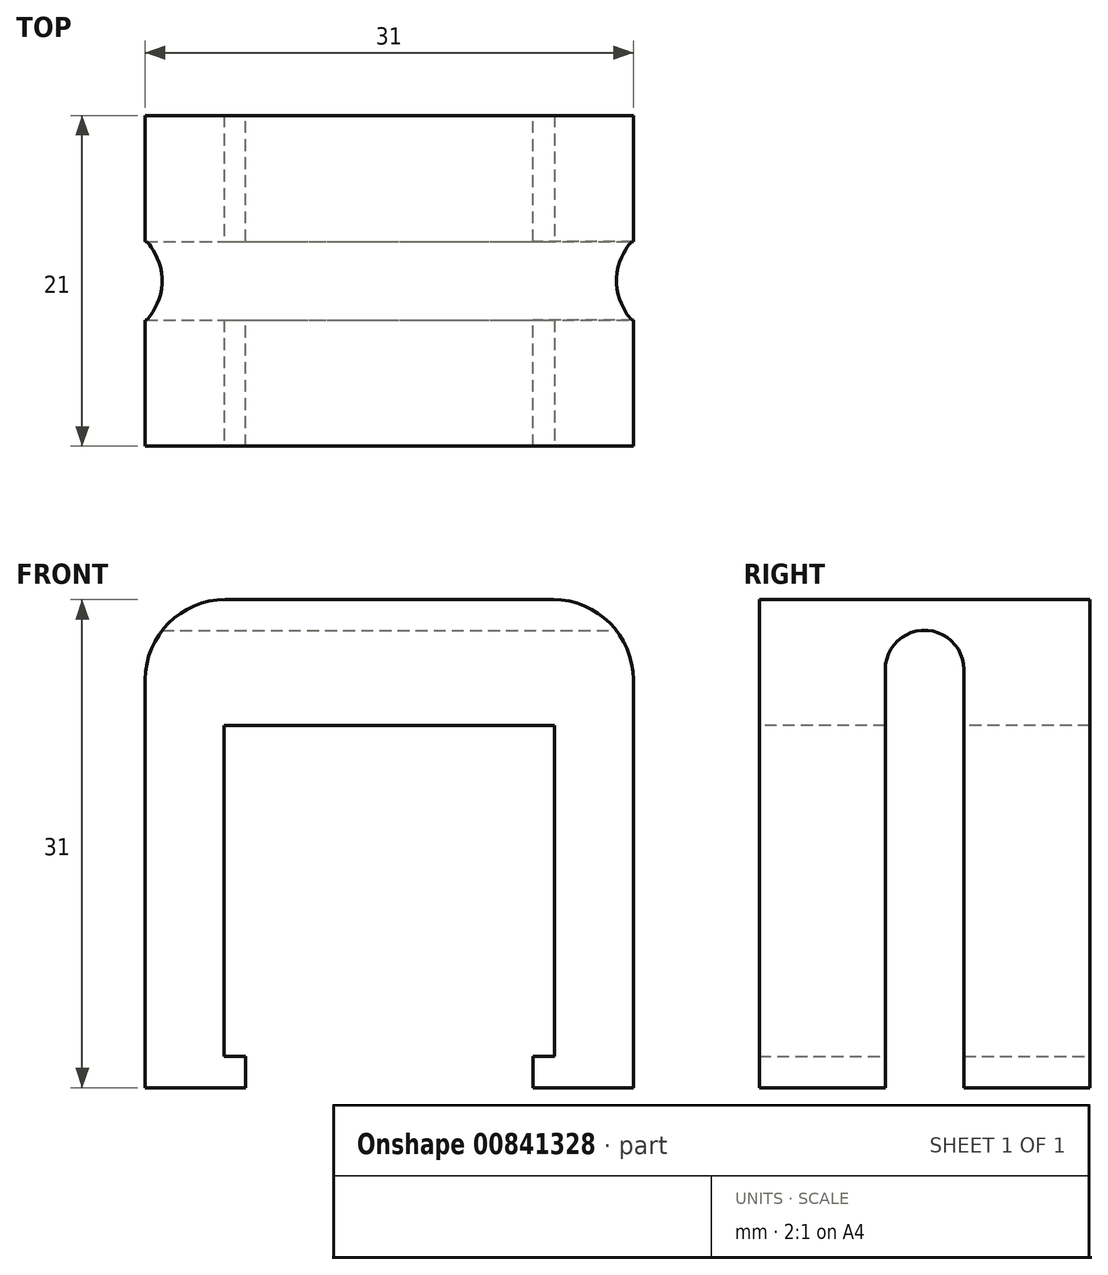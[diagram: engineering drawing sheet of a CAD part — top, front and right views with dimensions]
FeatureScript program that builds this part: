
annotation { "Feature Type Name" : "Feature", "Feature Type Description" : "" }
export const myFeature = defineFeature(function(context is Context, id is Id, definition is map)
    precondition{}
    {
        {
            var Q0;
            Q0=qCreatedBy(makeId("Top.planeOp"),FACE);
            var sketch = newSketch(context, id + "F0", { "sketchPlane" : qUnion([Q0])});
            skLineSegment(sketch, "E0.bottom", {"start": v(15.5, 10.5) * mm, "end": v(-15.5, 10.5) * mm});
            skLineSegment(sketch, "E0.top", {"start": v(15.5, -10.5) * mm, "end": v(-15.5, -10.5) * mm});
            skLineSegment(sketch, "E0.left", {"start": v(15.5, 10.5) * mm, "end": v(15.5, -10.5) * mm});
            skLineSegment(sketch, "E0.right", {"start": v(-15.5, 10.5) * mm, "end": v(-15.5, -10.5) * mm});
            skPoint(sketch, "E0.middle", {"position": v(0, 0) * mm});
            skSolve(sketch);
        }
        {
            var Q0;
            Q0=makeQuery(id+"F0.imprint","IMPRINT",FACE,{"disambiguationData":[TD([[makeQuery(id+"F0.imprint","IMPRINT",EDGE,{"derivedFrom":sQuery(id+"F0.wireOp",EDGE,"E0.bottom")}),1.0]])]});
            extrude(context, id + "F1", {"entities" : qUnion([Q0]), "depth" : 28 * mm, "offsetDistance" : 25.4 * mm});
        }
        {
            var Q0;
            Q0=qCreatedBy(makeId("Front.planeOp"),FACE);
            var sketch = newSketch(context, id + "F2", { "sketchPlane" : qUnion([Q0])});
            skLineSegment(sketch, "E1.bottom", {"start": v(10.5, 21) * mm, "end": v(-10.5, 21) * mm});
            skLineSegment(sketch, "E1.top", {"start": v(10.5, -21) * mm, "end": v(-10.5, -21) * mm});
            skLineSegment(sketch, "E1.left", {"start": v(10.5, 21) * mm, "end": v(10.5, -21) * mm});
            skLineSegment(sketch, "E1.right", {"start": v(-10.5, 21) * mm, "end": v(-10.5, -21) * mm});
            skPoint(sketch, "E1.middle", {"position": v(0, 0) * mm});
            skSolve(sketch);
        }
        {
            var Q0;
            Q0 = qSketchRegion(id + "F2", true);
            extrude(context, id + "F3", {"entities" : qUnion([Q0]), "operationType" : NewBodyOperationType.REMOVE, "oppositeDirection" : true, "depth" : 50.8 * mm, "offsetDistance" : 25.4 * mm});
        }
        {
            var Q0;
            Q0 = qSketchRegion(id + "F2", true);
            extrude(context, id + "F4", {"entities" : qUnion([Q0]), "operationType" : NewBodyOperationType.REMOVE, "depth" : 25.4 * mm, "offsetDistance" : 25.4 * mm});
        }
        {
            var Q0;
            Q0=qCreatedBy(makeId("Right.planeOp"),FACE);
            var sketch = newSketch(context, id + "F5", { "sketchPlane" : qUnion([Q0])});
            skCircle(sketch, "E2", {"center": v(0, 24.55) * mm, "radius": 2.5 * mm});
            skLineSegment(sketch, "E3.bottom", {"start": v(0, 24.55) * mm, "end": v(2.5, 24.55) * mm});
            skLineSegment(sketch, "E3.top", {"start": v(0, -28.56) * mm, "end": v(2.5, -28.56) * mm});
            skLineSegment(sketch, "E3.left", {"start": v(0, 24.55) * mm, "end": v(0, -28.56) * mm});
            skLineSegment(sketch, "E3.right", {"start": v(2.5, 24.55) * mm, "end": v(2.5, -28.56) * mm});
            skLineSegment(sketch, "E4.bottom", {"start": v(0, 24.55) * mm, "end": v(-2.5, 24.55) * mm});
            skLineSegment(sketch, "E4.top", {"start": v(0, -33.74) * mm, "end": v(-2.5, -33.74) * mm});
            skLineSegment(sketch, "E4.left", {"start": v(0, 24.55) * mm, "end": v(0, -33.74) * mm});
            skLineSegment(sketch, "E4.right", {"start": v(-2.5, 24.55) * mm, "end": v(-2.5, -33.74) * mm});
            skSolve(sketch);
        }
        {
            var Q0;
            Q0 = qSketchRegion(id + "F5", true);
            extrude(context, id + "F6", {"entities" : qUnion([Q0]), "operationType" : NewBodyOperationType.REMOVE, "oppositeDirection" : true, "depth" : 25.4 * mm, "offsetDistance" : 25.4 * mm});
        }
        {
            var Q0;
            Q0 = qSketchRegion(id + "F5", true);
            extrude(context, id + "F7", {"entities" : qUnion([Q0]), "operationType" : NewBodyOperationType.REMOVE, "depth" : 25.4 * mm, "offsetDistance" : 25.4 * mm});
        }
        {
            var Q0;
            {var subQ1=sQuery(id+"F0.wireOp",EDGE,"E0.left");var subQ2=sQuery(id+"F0.wireOp",EDGE,"E0.top");var subQ3=sQuery(id+"F0.wireOp",EDGE,"E0.bottom");Q0=makeQuery(id+"F4.boolean.opBoolean","SPLIT",FACE,{"disambiguationData":[TD([makeQuery(id+"F1.opExtrude","SWEPT_FACE",FACE,{"disambiguationData":[OSD([subQ1])]})])],"derivedFrom":makeQuery(id+"F1.opExtrude","CAP_FACE",FACE,{"disambiguationData":[OSD([subQ3,subQ2,subQ1,sQuery(id+"F0.wireOp",EDGE,"E0.right")])],"isStart":true})});}
            var Q1;
            {var subQ1=sQuery(id+"F0.wireOp",EDGE,"E0.top");var subQ2=sQuery(id+"F0.wireOp",EDGE,"E0.right");var subQ3=sQuery(id+"F0.wireOp",EDGE,"E0.bottom");Q1=makeQuery(id+"F4.boolean.opBoolean","SPLIT",FACE,{"disambiguationData":[TD([makeQuery(id+"F1.opExtrude","SWEPT_FACE",FACE,{"disambiguationData":[OSD([subQ2])]})])],"derivedFrom":makeQuery(id+"F1.opExtrude","CAP_FACE",FACE,{"disambiguationData":[OSD([subQ3,subQ1,sQuery(id+"F0.wireOp",EDGE,"E0.left"),subQ2])],"isStart":true})});}
            extrude(context, id + "F8", {"entities" : qUnion([Q0, Q1]), "operationType" : NewBodyOperationType.ADD, "depth" : 2 * mm, "offsetDistance" : 25.4 * mm});
        }
        {
            var Q0;
            Q0=qCreatedBy(makeId("Right.planeOp"),FACE);
            var sketch = newSketch(context, id + "F9", { "sketchPlane" : qUnion([Q0])});
            skLineSegment(sketch, "E5.bottom", {"start": v(0, 0) * mm, "end": v(-10.5, 0) * mm});
            skLineSegment(sketch, "E5.top", {"start": v(0, -2) * mm, "end": v(-10.5, -2) * mm});
            skLineSegment(sketch, "E5.left", {"start": v(0, 0) * mm, "end": v(0, -2) * mm});
            skLineSegment(sketch, "E5.right", {"start": v(-10.5, 0) * mm, "end": v(-10.5, -2) * mm});
            skLineSegment(sketch, "E6.bottom", {"start": v(0, 0) * mm, "end": v(10.5, 0) * mm});
            skLineSegment(sketch, "E6.top", {"start": v(0, -2) * mm, "end": v(10.5, -2) * mm});
            skLineSegment(sketch, "E6.right", {"start": v(10.5, 0) * mm, "end": v(10.5, -2) * mm});
            skSolve(sketch);
        }
        {
            var Q0;
            Q0=makeQuery(id+"F9.imprint","IMPRINT",FACE,{"disambiguationData":[TD([[makeQuery(id+"F9.imprint","IMPRINT",EDGE,{"derivedFrom":sQuery(id+"F9.wireOp",EDGE,"E5.bottom")}),1.0]])]});
            var Q1;
            Q1=makeQuery(id+"F9.imprint","IMPRINT",FACE,{"disambiguationData":[TD([[makeQuery(id+"F9.imprint","IMPRINT",EDGE,{"derivedFrom":sQuery(id+"F9.wireOp",EDGE,"E6.bottom")}),-1.0]])]});
            extrude(context, id + "F10", {"entities" : qUnion([Q0, Q1]), "operationType" : NewBodyOperationType.ADD, "depth" : 10.5 * mm, "offsetDistance" : 25.4 * mm});
        }
        {
            var Q0;
            Q0=makeQuery(id+"F10.opExtrude","CAP_FACE",FACE,{"disambiguationData":[OSD([sQuery(id+"F9.wireOp",EDGE,"E5.bottom"),sQuery(id+"F9.wireOp",EDGE,"E5.top"),sQuery(id+"F9.wireOp",EDGE,"E5.right"),sQuery(id+"F9.wireOp",EDGE,"E6.bottom"),sQuery(id+"F9.wireOp",EDGE,"E6.top"),sQuery(id+"F9.wireOp",EDGE,"E6.right")])],"isStart":true});
            extrude(context, id + "F11", {"entities" : qUnion([Q0]), "operationType" : NewBodyOperationType.ADD, "depth" : 10.5 * mm, "offsetDistance" : 25.4 * mm});
        }
        {
            var Q0;
            Q0=qCreatedBy(makeId("Top.planeOp"),FACE);
            var sketch = newSketch(context, id + "F12", { "sketchPlane" : qUnion([Q0])});
            skLineSegment(sketch, "E7.bottom", {"start": v(9.38, -24.95) * mm, "end": v(-9.38, -24.95) * mm});
            skLineSegment(sketch, "E7.top", {"start": v(9.38, 24.95) * mm, "end": v(-9.38, 24.95) * mm});
            skLineSegment(sketch, "E7.left", {"start": v(9.38, -24.95) * mm, "end": v(9.38, 24.95) * mm});
            skLineSegment(sketch, "E7.right", {"start": v(-9.38, -24.95) * mm, "end": v(-9.38, 24.95) * mm});
            skPoint(sketch, "E7.middle", {"position": v(0, 0) * mm});
            skSolve(sketch);
        }
        {
            var Q0;
            Q0=makeQuery(id+"F12.imprint","IMPRINT",FACE,{"disambiguationData":[TD([[makeQuery(id+"F12.imprint","IMPRINT",EDGE,{"derivedFrom":sQuery(id+"F12.wireOp",EDGE,"E7.bottom")}),-1.0]])]});
            extrude(context, id + "F13", {"entities" : qUnion([Q0]), "operationType" : NewBodyOperationType.REMOVE, "oppositeDirection" : true, "depth" : 25.4 * mm, "offsetDistance" : 25.4 * mm});
        }
        {
            var Q0;
            Q0=makeQuery(id+"F10.opExtrude","CAP_FACE",FACE,{"disambiguationData":[OSD([sQuery(id+"F9.wireOp",EDGE,"E5.bottom"),sQuery(id+"F9.wireOp",EDGE,"E5.top"),sQuery(id+"F9.wireOp",EDGE,"E5.right"),sQuery(id+"F9.wireOp",EDGE,"E6.bottom"),sQuery(id+"F9.wireOp",EDGE,"E6.top"),sQuery(id+"F9.wireOp",EDGE,"E6.right")])],"isStart":false});
            extrude(context, id + "F14", {"entities" : qUnion([Q0]), "operationType" : NewBodyOperationType.REMOVE, "oppositeDirection" : true, "depth" : 25.4 * mm, "offsetDistance" : 25.4 * mm});
        }
        {
            var Q0;
            {var subQ8=sQuery(id+"F0.wireOp",EDGE,"E0.bottom");var subQ9=makeQuery(id+"F1.opExtrude","SWEPT_FACE",FACE,{"disambiguationData":[OSD([subQ8])]});Q0=makeQuery(id+"F14.boolean.opBoolean","SPLIT",FACE,{"disambiguationData":[TD([subQ9])],"derivedFrom":makeQuery(id+"F13.boolean.opBoolean","COPY",FACE,{"derivedFrom":makeQuery(id+"F13.opExtrude","SWEPT_FACE",FACE,{"disambiguationData":[OSD([sQuery(id+"F12.wireOp",EDGE,"E7.left")])]})})});}
            var Q1;
            {var subQ6=sQuery(id+"F0.wireOp",EDGE,"E0.top");var subQ7=makeQuery(id+"F1.opExtrude","SWEPT_FACE",FACE,{"disambiguationData":[OSD([subQ6])]});Q1=makeQuery(id+"F14.boolean.opBoolean","SPLIT",FACE,{"disambiguationData":[TD([subQ7])],"derivedFrom":makeQuery(id+"F13.boolean.opBoolean","COPY",FACE,{"derivedFrom":makeQuery(id+"F13.opExtrude","SWEPT_FACE",FACE,{"disambiguationData":[OSD([sQuery(id+"F12.wireOp",EDGE,"E7.left")])]})})});}
            extrude(context, id + "F15", {"entities" : qUnion([Q0, Q1]), "operationType" : NewBodyOperationType.ADD, "depth" : .25 * mm, "offsetDistance" : 25.4 * mm});
        }
        {
            var Q0;
            {var subQ8=sQuery(id+"F0.wireOp",EDGE,"E0.bottom");var subQ9=makeQuery(id+"F1.opExtrude","SWEPT_FACE",FACE,{"disambiguationData":[OSD([subQ8])]});Q0=makeQuery(id+"F14.boolean.opBoolean","SPLIT",FACE,{"disambiguationData":[TD([subQ9])],"derivedFrom":makeQuery(id+"F13.boolean.opBoolean","COPY",FACE,{"derivedFrom":makeQuery(id+"F13.opExtrude","SWEPT_FACE",FACE,{"disambiguationData":[OSD([sQuery(id+"F12.wireOp",EDGE,"E7.right")])]})})});}
            var Q1;
            {var subQ6=sQuery(id+"F0.wireOp",EDGE,"E0.top");var subQ7=makeQuery(id+"F1.opExtrude","SWEPT_FACE",FACE,{"disambiguationData":[OSD([subQ6])]});Q1=makeQuery(id+"F14.boolean.opBoolean","SPLIT",FACE,{"disambiguationData":[TD([subQ7])],"derivedFrom":makeQuery(id+"F13.boolean.opBoolean","COPY",FACE,{"derivedFrom":makeQuery(id+"F13.opExtrude","SWEPT_FACE",FACE,{"disambiguationData":[OSD([sQuery(id+"F12.wireOp",EDGE,"E7.right")])]})})});}
            extrude(context, id + "F16", {"entities" : qUnion([Q0, Q1]), "operationType" : NewBodyOperationType.ADD, "depth" : .25 * mm, "offsetDistance" : 25.4 * mm});
        }
        {
            var Q0;
            Q0=makeQuery(id+"F1.opExtrude","CAP_FACE",FACE,{"disambiguationData":[OSD([sQuery(id+"F0.wireOp",EDGE,"E0.bottom"),sQuery(id+"F0.wireOp",EDGE,"E0.top"),sQuery(id+"F0.wireOp",EDGE,"E0.left"),sQuery(id+"F0.wireOp",EDGE,"E0.right")])],"isStart":false});
            extrude(context, id + "F17", {"entities" : qUnion([Q0]), "operationType" : NewBodyOperationType.ADD, "depth" : 1 * mm, "offsetDistance" : 25.4 * mm});
        }
        {
            var Q0;
            Q0=makeQuery(id+"F17.opExtrude","CAP_EDGE",EDGE,{"disambiguationData":[OSD([sQuery(id+"F0.wireOp",EDGE,"E0.right")])],"isStart":false});
            var Q1;
            Q1=makeQuery(id+"F17.opExtrude","CAP_EDGE",EDGE,{"disambiguationData":[OSD([sQuery(id+"F0.wireOp",EDGE,"E0.left")])],"isStart":false});
            fillet(context, id + "F18", {"entities" : qUnion([Q0, Q1]), "radius" : 5.08 * mm, "tangentPropagation" : true, "allowEdgeOverflow" : false});
        }
    });
